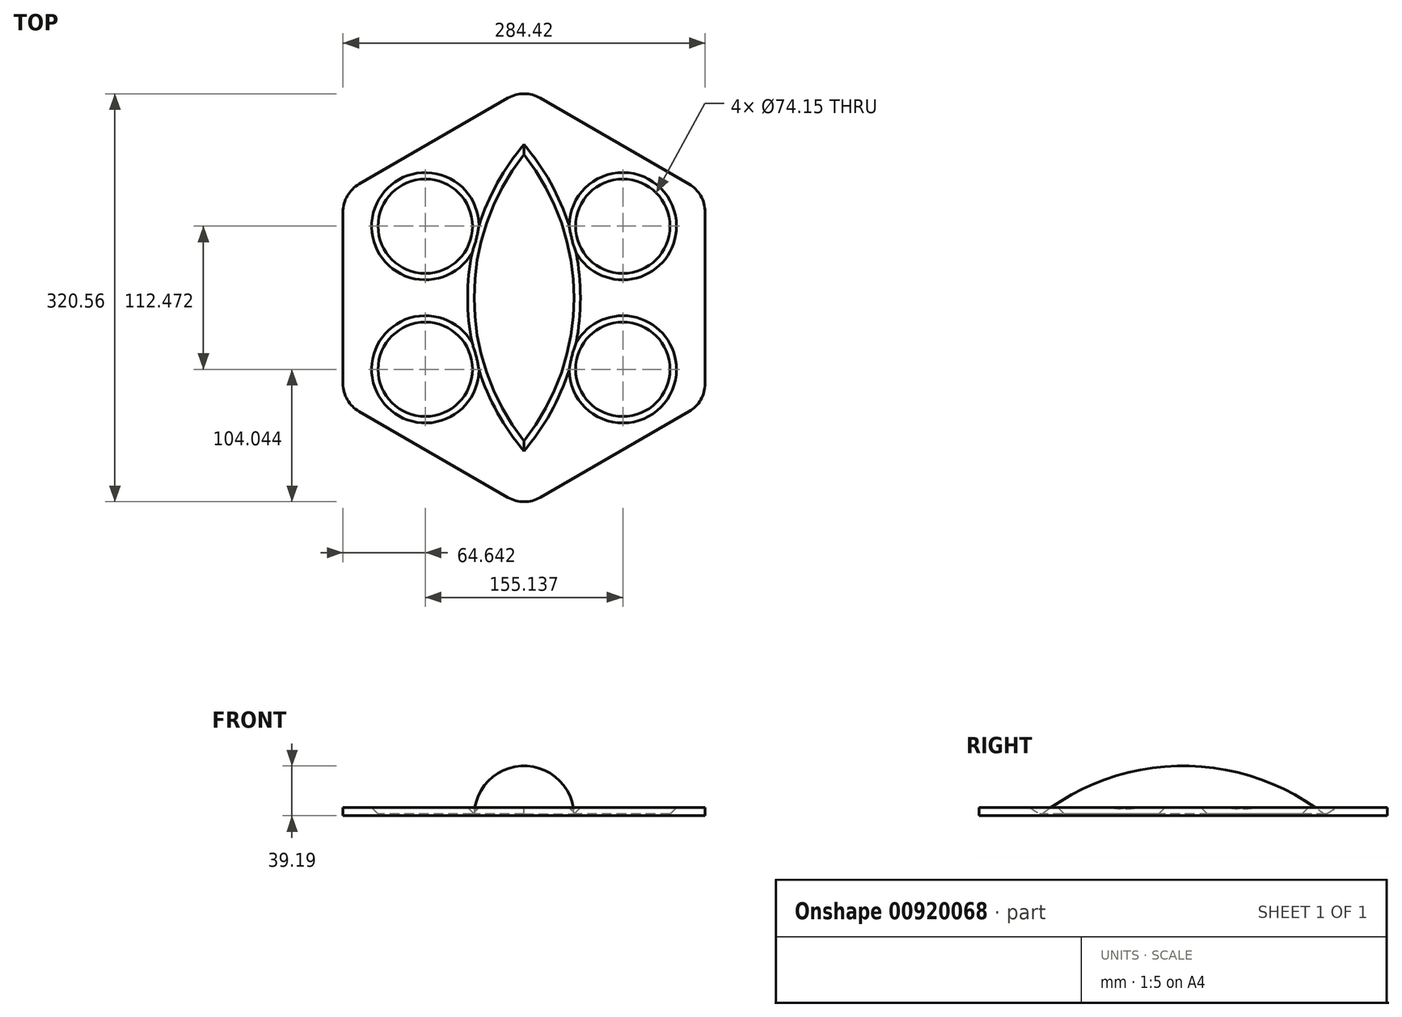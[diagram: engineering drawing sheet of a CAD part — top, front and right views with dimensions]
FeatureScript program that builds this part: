
annotation { "Feature Type Name" : "Feature", "Feature Type Description" : "" }
export const myFeature = defineFeature(function(context is Context, id is Id, definition is map)
    precondition{}
    {
        {
            var Q0;
            Q0=qCreatedBy(makeId("Top.planeOp"),FACE);
            var sketch = newSketch(context, id + "F0", { "sketchPlane" : qUnion([Q0])});
            skLineSegment(sketch, "E0", {"start": v(0, 0) * mm, "end": v(0, 112.47) * mm});
            skLineSegment(sketch, "E1", {"start": v(0, 0) * mm, "end": v(-142.2, 0) * mm});
            skCircle(sketch, "E2", {"center": v(-77.57, 56.24) * mm, "radius": 37.08 * mm});
            skPoint(sketch, "E2.centerSnap0", {"position": v(0, 56.24) * mm});
            skCircle(sketch, "E3.MirrorC", {"center": v(-77.57, -56.24) * mm, "radius": 37.08 * mm});
            skCircle(sketch, "E4.MirrorC", {"center": v(77.57, 56.24) * mm, "radius": 37.08 * mm});
            skCircle(sketch, "E5.MirrorC", {"center": v(77.57, -56.24) * mm, "radius": 37.08 * mm});
            skLineSegment(sketch, "E6.MirrorCS", {"start": v(0, 0) * mm, "end": v(0, -112.47) * mm});
            skCircle(sketch, "E7.cCircle", {"center": v(0, 0) * mm, "radius": 142.2 * mm, "construction": true});
            skLineSegment(sketch, "E7.0", {"start": v(-142.2, -67.44) * mm, "end": v(-142.2, 67.44) * mm});
            skLineSegment(sketch, "E7.1", {"start": v(-129.5, 89.44) * mm, "end": v(-12.7, 156.87) * mm});
            skLineSegment(sketch, "E7.2", {"start": v(12.7, 156.87) * mm, "end": v(129.5, 89.44) * mm});
            skLineSegment(sketch, "E7.3", {"start": v(142.2, 67.44) * mm, "end": v(142.2, -67.44) * mm});
            skLineSegment(sketch, "E7.4", {"start": v(129.5, -89.44) * mm, "end": v(12.7, -156.87) * mm});
            skLineSegment(sketch, "E7.5", {"start": v(-12.7, -156.87) * mm, "end": v(-129.5, -89.44) * mm});
            skPoint(sketch, "E7.0.midPoint", {"position": v(-142.2, 0) * mm});
            skArc(sketch, "E8.trimOffspring", {"start": v(-42.67, -43.72) * mm, "mid": v(-42.08, -45.76) * mm, "end": v(-41.47, -47.8) * mm});
            skArc(sketch, "E9", {"start": v(0, 112.47) * mm, "mid": v(-39.2, 0) * mm, "end": v(0, -112.47) * mm});
            skArc(sketch, "E10.MirrorCS", {"start": v(0, 112.47) * mm, "mid": v(39.2, 0) * mm, "end": v(0, -112.47) * mm});
            skPoint(sketch, "E11.visualSharp", {"position": v(-142.2, -82.1) * mm});
            skArc(sketch, "E11.filletArc", {"start": v(-142.2, -67.44) * mm, "mid": v(-138.8, -80.14) * mm, "end": v(-129.5, -89.44) * mm});
            skPoint(sketch, "E12.visualSharp", {"position": v(-142.2, 82.1) * mm});
            skArc(sketch, "E12.filletArc", {"start": v(-129.5, 89.44) * mm, "mid": v(-138.8, 80.14) * mm, "end": v(-142.2, 67.44) * mm});
            skPoint(sketch, "E13.visualSharp", {"position": v(0, 164.2) * mm});
            skArc(sketch, "E13.filletArc", {"start": v(12.7, 156.87) * mm, "mid": v(0, 160.28) * mm, "end": v(-12.7, 156.87) * mm});
            skPoint(sketch, "E14.visualSharp", {"position": v(0, -164.2) * mm});
            skArc(sketch, "E14.filletArc", {"start": v(-12.7, -156.87) * mm, "mid": v(0, -160.28) * mm, "end": v(12.7, -156.87) * mm});
            skPoint(sketch, "E15.visualSharp", {"position": v(142.2, -82.1) * mm});
            skArc(sketch, "E15.filletArc", {"start": v(129.5, -89.44) * mm, "mid": v(138.8, -80.14) * mm, "end": v(142.2, -67.44) * mm});
            skPoint(sketch, "E16.visualSharp", {"position": v(142.2, 82.1) * mm});
            skArc(sketch, "E16.filletArc", {"start": v(142.2, 67.44) * mm, "mid": v(138.8, 80.14) * mm, "end": v(129.5, 89.44) * mm});
            skSolve(sketch);
        }
        {
            var Q0;
            Q0=makeQuery(id+"F0.imprint","IMPRINT",FACE,{"disambiguationData":[TD([[makeQuery(id+"F0.imprint","IMPRINT",EDGE,{"derivedFrom":sQuery(id+"F0.wireOp",EDGE,"E0")}),-1.0]])]});
            var Q1;
            Q1=sQuery(id+"F0.wireOp",EDGE,"E6.MirrorCS");
            revolve(context, id + "F1", {"surfaceOperationType" : NewSurfaceOperationType.NEW, "entities" : qUnion([Q0]), "axis" : qUnion([Q1]), "revolveType" : RevolveType.ONE_DIRECTION, "angle" : 180 * degree});
        }
        {
            var Q0;
            Q0=makeQuery(id+"F0.imprint","IMPRINT",FACE,{"disambiguationData":[TD([[makeQuery(id+"F0.imprint","IMPRINT",EDGE,{"derivedFrom":sQuery(id+"F0.wireOp",EDGE,"E2")}),-1.0]])]});
            extrude(context, id + "F2", {"entities" : qUnion([Q0]), "depth" : 6.35 * mm, "offsetDistance" : 25.4 * mm});
        }
        {
            var Q0;
            Q0=makeQuery(id+"F2.opExtrude","CAP_EDGE",EDGE,{"disambiguationData":[OSD([sQuery(id+"F0.wireOp",EDGE,"E10.MirrorCS")])],"isStart":false});
            var Q1;
            Q1=makeQuery(id+"F2.opExtrude","CAP_EDGE",EDGE,{"disambiguationData":[OSD([sQuery(id+"F0.wireOp",EDGE,"E9")])],"isStart":false});
            chamfer(context, id + "F3", {"entities" : qUnion([Q0, Q1]), "width" : 5.08 * mm, "tangentPropagation" : true});
        }
        {
            var Q0;
            Q0=makeQuery(id+"F2.opExtrude","CAP_EDGE",EDGE,{"disambiguationData":[OSD([sQuery(id+"F0.wireOp",EDGE,"E2")])],"isStart":false});
            var Q1;
            Q1=makeQuery(id+"F2.opExtrude","CAP_EDGE",EDGE,{"disambiguationData":[OSD([sQuery(id+"F0.wireOp",EDGE,"E3.MirrorC")])],"isStart":false});
            var Q2;
            Q2=makeQuery(id+"F2.opExtrude","CAP_EDGE",EDGE,{"disambiguationData":[OSD([sQuery(id+"F0.wireOp",EDGE,"E4.MirrorC")])],"isStart":false});
            var Q3;
            Q3=makeQuery(id+"F2.opExtrude","CAP_EDGE",EDGE,{"disambiguationData":[OSD([sQuery(id+"F0.wireOp",EDGE,"E5.MirrorC")])],"isStart":false});
            chamfer(context, id + "F4", {"entities" : qUnion([Q0, Q1, Q2, Q3]), "width" : 5.08 * mm, "tangentPropagation" : true});
        }
    });
